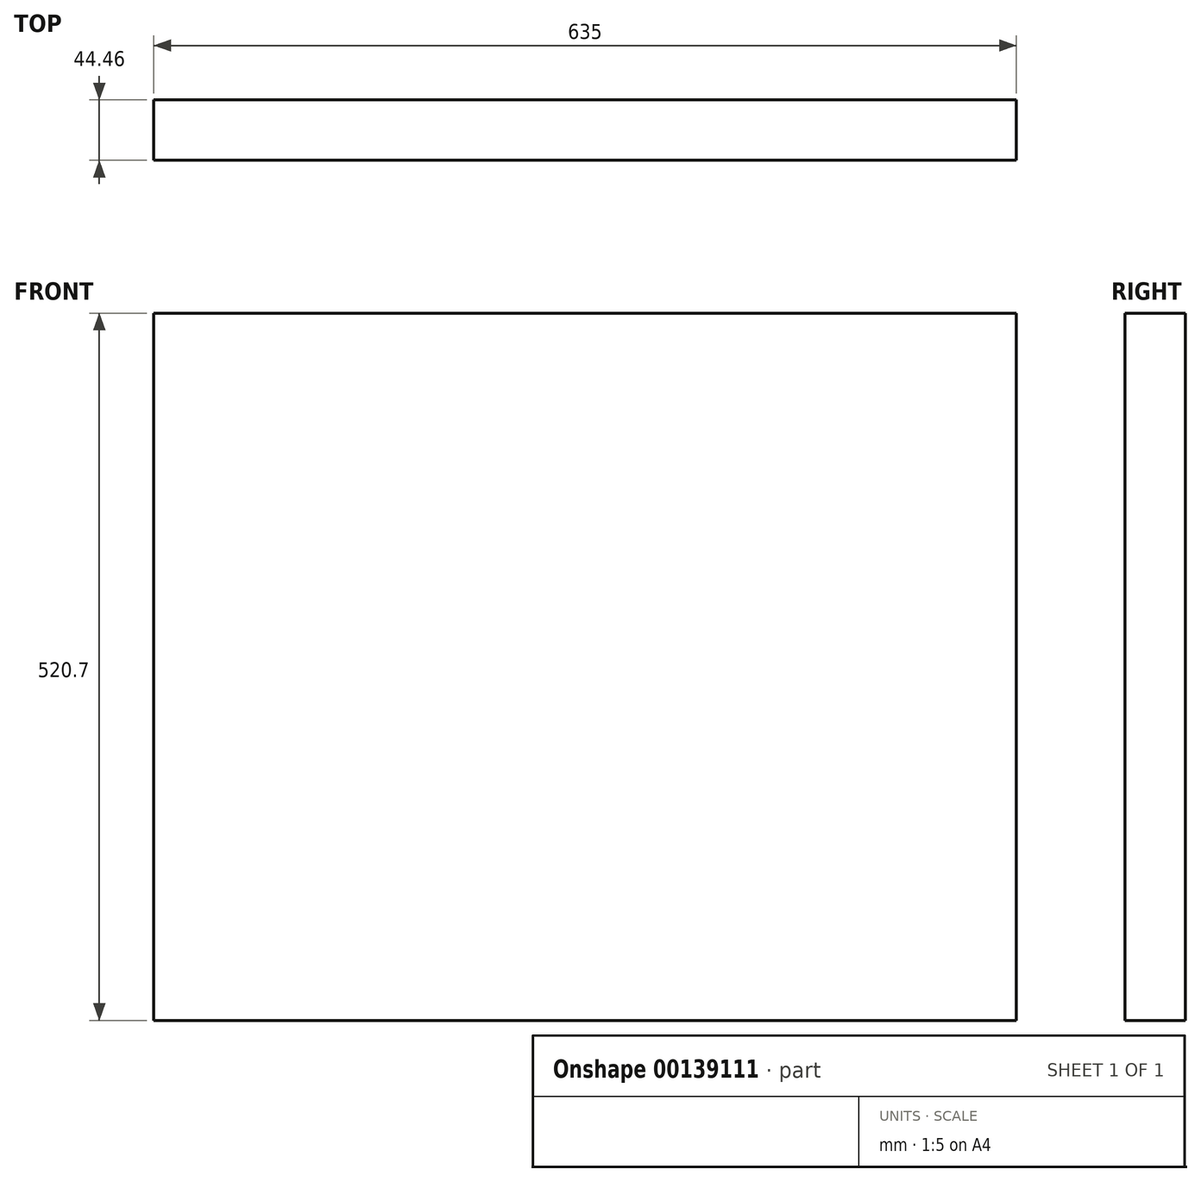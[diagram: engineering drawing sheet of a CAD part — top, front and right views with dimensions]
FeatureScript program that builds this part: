
annotation { "Feature Type Name" : "Feature", "Feature Type Description" : "" }
export const myFeature = defineFeature(function(context is Context, id is Id, definition is map)
    precondition{}
    {
        {
            var Q0;
            Q0=qCreatedBy(makeId("Front.planeOp"),FACE);
            var sketch = newSketch(context, id + "F0", { "sketchPlane" : qUnion([Q0])});
            skLineSegment(sketch, "E0.bottom", {"start": v(-353.13, 476.96) * mm, "end": v(281.87, 476.96) * mm});
            skLineSegment(sketch, "E0.top", {"start": v(-353.13, -43.74) * mm, "end": v(281.87, -43.74) * mm});
            skLineSegment(sketch, "E0.left", {"start": v(-353.13, 476.96) * mm, "end": v(-353.13, -43.74) * mm});
            skLineSegment(sketch, "E0.right", {"start": v(281.87, 476.96) * mm, "end": v(281.87, -43.74) * mm});
            skSolve(sketch);
        }
        {
            var Q0;
            Q0=makeQuery(id+"F0.imprint","IMPRINT",FACE,{"disambiguationData":[TD([[makeQuery(id+"F0.imprint","IMPRINT",EDGE,{"derivedFrom":sQuery(id+"F0.wireOp",EDGE,"E0.bottom")}),-1.0]])]});
            extrude(context, id + "F1", {"entities" : qUnion([Q0]), "endBound" : BoundingType.SYMMETRIC, "depth" : 44.45 * mm});
        }
    });
